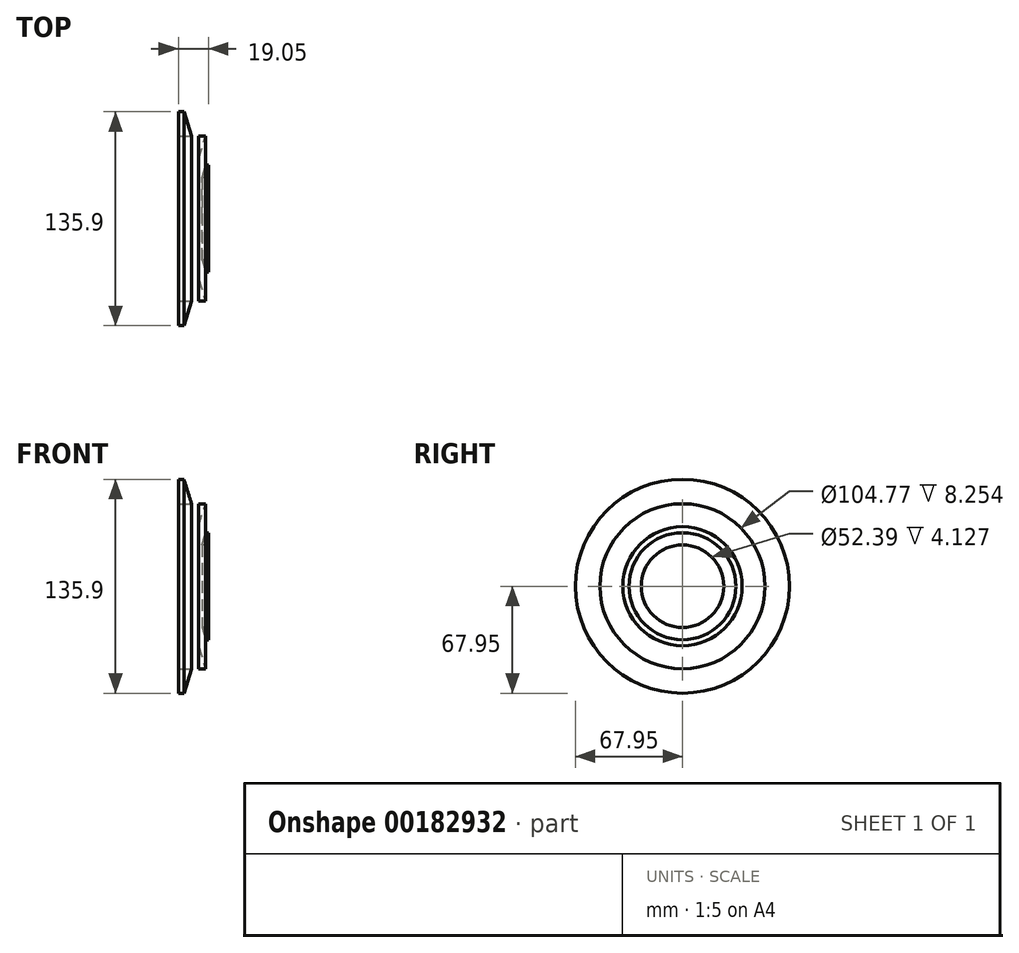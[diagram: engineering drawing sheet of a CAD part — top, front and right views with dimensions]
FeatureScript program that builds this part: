
annotation { "Feature Type Name" : "Feature", "Feature Type Description" : "" }
export const myFeature = defineFeature(function(context is Context, id is Id, definition is map)
    precondition{}
    {
        {
            var Q0;
            Q0=qCreatedBy(makeId("Front.planeOp"),FACE);
            var sketch = newSketch(context, id + "F0", { "sketchPlane" : qUnion([Q0])});
            skLineSegment(sketch, "E0", {"start": v(0, 0) * mm, "end": v(0, 52.39) * mm});
            skLineSegment(sketch, "E1.0", {"start": v(12.7, 0) * mm, "end": v(12.7, 67.94) * mm});
            skLineSegment(sketch, "E2", {"start": v(9.2, 67.95) * mm, "end": v(0, 37.85) * mm});
            skLineSegment(sketch, "E3", {"start": v(9.2, 67.94) * mm, "end": v(12.7, 67.94) * mm});
            skLineSegment(sketch, "E4.0", {"start": v(0, 52.39) * mm, "end": v(12.7, 52.39) * mm});
            skLineSegment(sketch, "E5", {"start": v(0, 37.85) * mm, "end": v(0, 0) * mm});
            skLineSegment(sketch, "E6", {"start": v(0, 0) * mm, "end": v(42.96, 0) * mm});
            skSolve(sketch);
        }
        {
            var Q0;
            {var subQ0=sQuery(id+"F0.wireOp",EDGE,"E5");Q0=makeQuery(id+"F0.imprint","IMPRINT",FACE,{"disambiguationData":[TD([[makeQuery(id+"F0.imprint","IMPRINT",EDGE,{"derivedFrom":subQ0}),1.0]])]});}
            var Q1;
            {var subQ0=sQuery(id+"F0.wireOp",EDGE,"E0");Q1=makeQuery(id+"F0.imprint","IMPRINT",FACE,{"disambiguationData":[TD([[makeQuery(id+"F0.imprint","IMPRINT",EDGE,{"derivedFrom":subQ0}),-1.0]])]});}
            var Q2;
            {var subQ0=sQuery(id+"F0.wireOp",EDGE,"E3");Q2=makeQuery(id+"F0.imprint","IMPRINT",FACE,{"disambiguationData":[TD([[makeQuery(id+"F0.imprint","IMPRINT",EDGE,{"derivedFrom":subQ0}),-1.0]])]});}
            var Q3;
            Q3=sQuery(id+"F0.wireOp",EDGE,"E6");
            revolve(context, id + "F1", {"entities" : qUnion([Q0, Q1, Q2]), "axis" : qUnion([Q3]), "revolveType" : RevolveType.FULL});
        }
        {
            var Q0;
            Q0=makeQuery(id+"F1.opRevolve","SWEPT_FACE",FACE,{"disambiguationData":[OSD([sQuery(id+"F0.wireOp",EDGE,"E0"),sQuery(id+"F0.wireOp",EDGE,"E5")])]});
            var sketch = newSketch(context, id + "F2", { "sketchPlane" : qUnion([Q0])});
            skCircle(sketch, "E7", {"center": v(0, 0) * mm, "radius": 17.5 * mm});
            skSolve(sketch);
        }
        {
            var Q0;
            Q0=qSketchRegion(id+"F2",true);
            extrude(context, id + "F3", {"entities" : qUnion([Q0]), "operationType" : NewBodyOperationType.REMOVE, "oppositeDirection" : true, "depth" : 25 * mm});
        }
        {
            var Q0;
            Q0=makeQuery(id+"F1.opRevolve","SWEPT_BODY",BODY,{"disambiguationData":[OSD([sQuery(id+"F0.wireOp",EDGE,"E0"),sQuery(id+"F0.wireOp",EDGE,"E1.0"),sQuery(id+"F0.wireOp",EDGE,"E2"),sQuery(id+"F0.wireOp",EDGE,"E3"),sQuery(id+"F0.wireOp",EDGE,"E4.0"),sQuery(id+"F0.wireOp",EDGE,"E5"),sQuery(id+"F0.wireOp",EDGE,"E6")])]});
            var Q1;
            Q1=qCreatedBy(makeId("Right.planeOp"),FACE);
            mirror(context, id + "F4", {"operationType" : NewBodyOperationType.ADD, "entities" : qUnion([Q0]), "mirrorPlane" : qUnion([Q1])});
        }
        {
            var Q0;
            Q0=makeQuery(id+"F1.opRevolve","SWEPT_BODY",BODY,{"disambiguationData":[OSD([sQuery(id+"F0.wireOp",EDGE,"E0"),sQuery(id+"F0.wireOp",EDGE,"E1.0"),sQuery(id+"F0.wireOp",EDGE,"E2"),sQuery(id+"F0.wireOp",EDGE,"E3"),sQuery(id+"F0.wireOp",EDGE,"E4.0"),sQuery(id+"F0.wireOp",EDGE,"E5"),sQuery(id+"F0.wireOp",EDGE,"E6")])]});
            var Q1;
            Q1=qCreatedBy(makeId("Origin.pointOp"),VERTEX);
            transform(context, id + "F5", {"entities" : qUnion([Q0]), "transformType" : TransformType.SCALE_UNIFORMLY, "scale" : 0.5, "scalePoint" : qUnion([Q1]), "makeCopy" : false});
        }
    });
